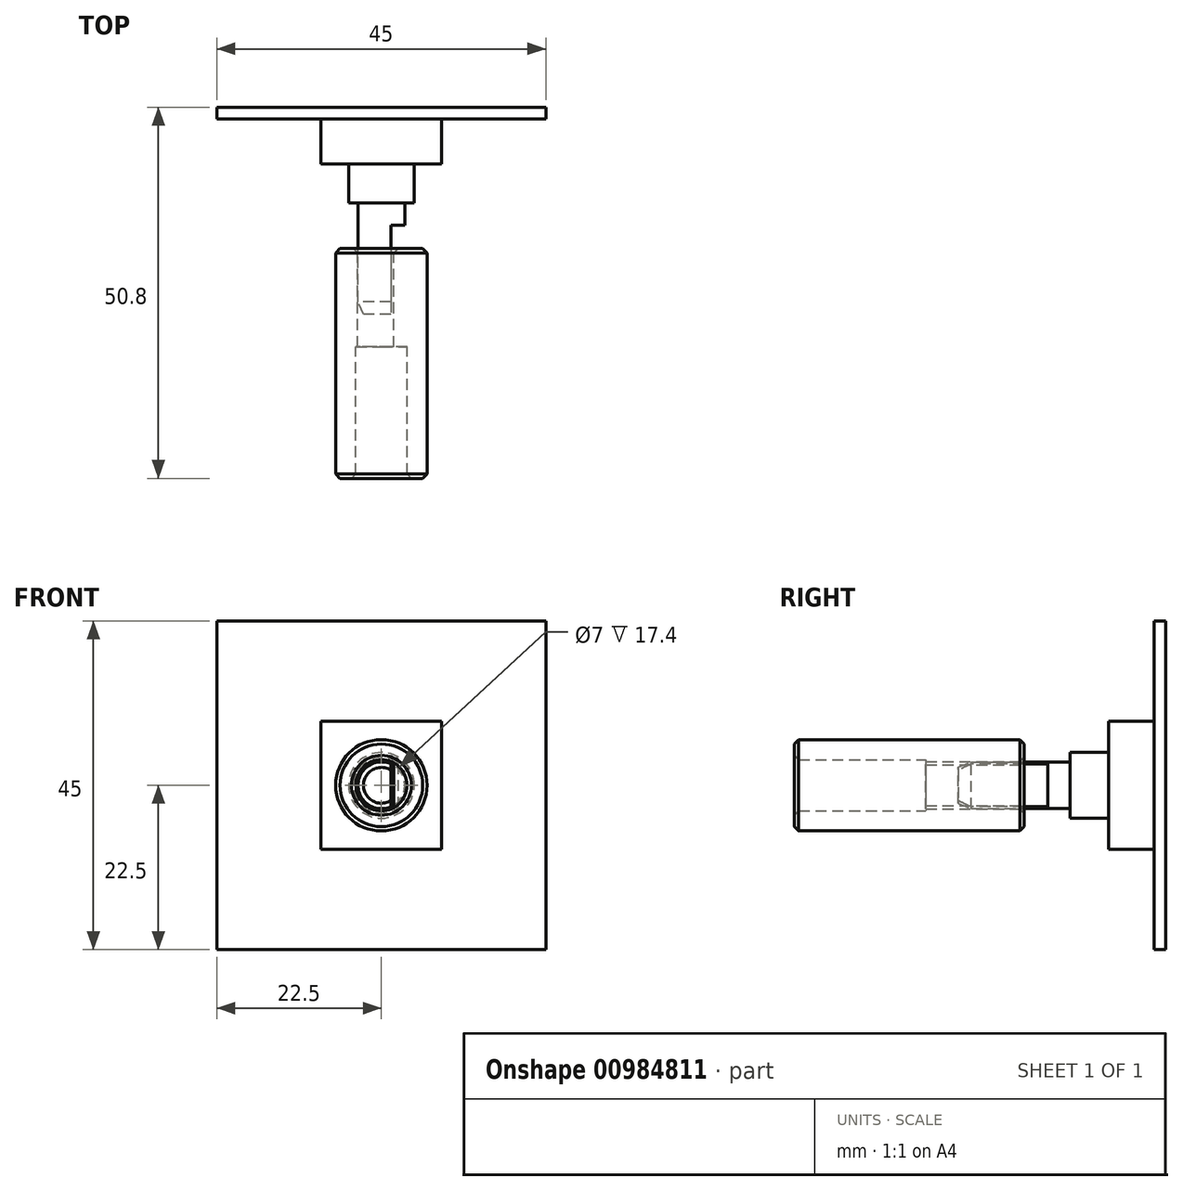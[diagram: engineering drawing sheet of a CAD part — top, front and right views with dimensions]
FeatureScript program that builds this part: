
annotation { "Feature Type Name" : "Feature", "Feature Type Description" : "" }
export const myFeature = defineFeature(function(context is Context, id is Id, definition is map)
    precondition{}
    {
        {
            var Q0;
            Q0=qCreatedBy(makeId("Front.planeOp"),FACE);
            var sketch = newSketch(context, id + "F0", { "sketchPlane" : qUnion([Q0])});
            skLineSegment(sketch, "E0.bottom", {"start": v(22.5, 22.5) * mm, "end": v(-22.5, 22.5) * mm});
            skLineSegment(sketch, "E0.top", {"start": v(22.5, -22.5) * mm, "end": v(-22.5, -22.5) * mm});
            skLineSegment(sketch, "E0.left", {"start": v(22.5, 22.5) * mm, "end": v(22.5, -22.5) * mm});
            skLineSegment(sketch, "E0.right", {"start": v(-22.5, 22.5) * mm, "end": v(-22.5, -22.5) * mm});
            skPoint(sketch, "E0.middle", {"position": v(0, 0) * mm});
            skSolve(sketch);
        }
        {
            var Q0;
            Q0 = qSketchRegion(id + "F0", true);
            extrude(context, id + "F1", {"entities" : qUnion([Q0]), "oppositeDirection" : true, "depth" : 1.6 * mm, "offsetDistance" : 25 * mm});
        }
        {
            var Q0;
            Q0=makeQuery(id+"F1.opExtrude","CAP_FACE",FACE,{"disambiguationData":[OSD([sQuery(id+"F0.wireOp",EDGE,"E0.bottom"),sQuery(id+"F0.wireOp",EDGE,"E0.top"),sQuery(id+"F0.wireOp",EDGE,"E0.left"),sQuery(id+"F0.wireOp",EDGE,"E0.right")])],"isStart":true});
            var sketch = newSketch(context, id + "F2", { "sketchPlane" : qUnion([Q0])});
            skLineSegment(sketch, "E1.bottom", {"start": v(8.25, 8.75) * mm, "end": v(-8.25, 8.75) * mm});
            skLineSegment(sketch, "E1.top", {"start": v(8.25, -8.75) * mm, "end": v(-8.25, -8.75) * mm});
            skLineSegment(sketch, "E1.left", {"start": v(8.25, 8.75) * mm, "end": v(8.25, -8.75) * mm});
            skLineSegment(sketch, "E1.right", {"start": v(-8.25, 8.75) * mm, "end": v(-8.25, -8.75) * mm});
            skPoint(sketch, "E1.middle", {"position": v(0, 0) * mm});
            skSolve(sketch);
        }
        {
            var Q0;
            Q0 = qSketchRegion(id + "F2", true);
            extrude(context, id + "F3", {"entities" : qUnion([Q0]), "operationType" : NewBodyOperationType.ADD, "depth" : 6.2 * mm, "offsetDistance" : 25 * mm});
        }
        {
            var Q0;
            Q0=makeQuery(id+"F3.opExtrude","CAP_FACE",FACE,{"disambiguationData":[OSD([sQuery(id+"F2.wireOp",EDGE,"E1.bottom"),sQuery(id+"F2.wireOp",EDGE,"E1.top"),sQuery(id+"F2.wireOp",EDGE,"E1.left"),sQuery(id+"F2.wireOp",EDGE,"E1.right")])],"isStart":false});
            var sketch = newSketch(context, id + "F4", { "sketchPlane" : qUnion([Q0])});
            skCircle(sketch, "E2", {"center": v(0, 0) * mm, "radius": 4.5 * mm});
            skSolve(sketch);
        }
        {
            var Q0;
            Q0 = qSketchRegion(id + "F4", true);
            extrude(context, id + "F5", {"entities" : qUnion([Q0]), "operationType" : NewBodyOperationType.ADD, "depth" : 5.3 * mm, "offsetDistance" : 25 * mm});
        }
        {
            var Q0;
            Q0=makeQuery(id+"F5.opExtrude","CAP_FACE",FACE,{"disambiguationData":[OSD([sQuery(id+"F4.wireOp",EDGE,"E2")])],"isStart":false});
            var sketch = newSketch(context, id + "F6", { "sketchPlane" : qUnion([Q0])});
            skCircle(sketch, "E3", {"center": v(0, 0) * mm, "radius": 3.2 * mm});
            skSolve(sketch);
        }
        {
            var Q0;
            Q0 = qSketchRegion(id + "F6", true);
            extrude(context, id + "F7", {"entities" : qUnion([Q0]), "operationType" : NewBodyOperationType.ADD, "depth" : 15.25 * mm, "offsetDistance" : 25 * mm});
        }
        {
            var Q0;
            Q0=makeQuery(id+"F7.opExtrude","CAP_FACE",FACE,{"disambiguationData":[OSD([sQuery(id+"F6.wireOp",EDGE,"E3")])],"isStart":false});
            var sketch = newSketch(context, id + "F8", { "sketchPlane" : qUnion([Q0])});
            skArc(sketch, "E4.1", {"start": v(1.3, -2.92) * mm, "mid": v(3.2, 0) * mm, "end": v(1.3, 2.92) * mm});
            skLineSegment(sketch, "E5", {"start": v(1.3, 2.92) * mm, "end": v(1.3, -2.92) * mm});
            skSolve(sketch);
        }
        {
            var Q0;
            Q0 = qSketchRegion(id + "F8", true);
            extrude(context, id + "F9", {"entities" : qUnion([Q0]), "operationType" : NewBodyOperationType.REMOVE, "oppositeDirection" : true, "depth" : 12.2 * mm, "offsetDistance" : 25 * mm});
        }
        {
            var Q0;
            Q0=qCreatedBy(makeId("Top.planeOp"),FACE);
            var sketch = newSketch(context, id + "F10", { "sketchPlane" : qUnion([Q0])});
            skLineSegment(sketch, "E6", {"start": v(-3.2, -25) * mm, "end": v(-3.2, -26.75) * mm});
            skLineSegment(sketch, "E7", {"start": v(-3.2, -26.75) * mm, "end": v(-2.45, -26.75) * mm});
            skLineSegment(sketch, "E8", {"start": v(-2.45, -26.75) * mm, "end": v(-3.2, -25) * mm});
            skLineSegment(sketch, "E9", {"start": v(0, -26.75) * mm, "end": v(0, 0) * mm, "construction": true});
            skSolve(sketch);
        }
        {
            var Q0;
            Q0 = qSketchRegion(id + "F10", true);
            var Q1;
            Q1=sQuery(id+"F10.wireOp",EDGE,"E9");
            var Q2;
            Q2=sQuery(id+"F10.wireOp",EDGE,"E6");
            var Q3;
            Q3=sQuery(id+"F10.wireOp",EDGE,"E8");
            var Q4;
            Q4=sQuery(id+"F10.wireOp",EDGE,"E7");
            var Q5;
            Q5=sQuery(id+"F10.wireOp",EDGE,"E9");
            revolve(context, id + "F11", {"operationType" : NewBodyOperationType.REMOVE, "surfaceOperationType" : NewSurfaceOperationType.NEW, "entities" : qUnion([Q0]), "surfaceEntities" : qUnion([Q1, Q2, Q3, Q4]), "axis" : qUnion([Q5]), "revolveType" : RevolveType.FULL, "oppositeDirection" : true});
        }
        {
            var Q0;
            Q0=qCreatedBy(makeId("Right.planeOp"),FACE);
            var sketch = newSketch(context, id + "F12", { "sketchPlane" : qUnion([Q0])});
            skLineSegment(sketch, "E10", {"start": v(0, 0) * mm, "end": v(-106.64, 0) * mm, "construction": true});
            skLineSegment(sketch, "E11", {"start": v(-73.58, -21.29) * mm, "end": v(-73.58, 21.29) * mm, "construction": true});
            skPoint(sketch, "E12", {"position": v(-73.58, 0) * mm});
            skLineSegment(sketch, "E13.bottom", {"start": v(-47.64, -8) * mm, "end": v(-42.64, -8) * mm});
            skLineSegment(sketch, "E13.top", {"start": v(-47.64, 8) * mm, "end": v(-42.64, 8) * mm});
            skLineSegment(sketch, "E13.left", {"start": v(-47.64, -8) * mm, "end": v(-47.64, 8) * mm});
            skLineSegment(sketch, "E13.right", {"start": v(-42.64, -8) * mm, "end": v(-42.64, 8) * mm});
            skPoint(sketch, "E13.middle", {"position": v(-45.14, 0) * mm});
            skLineSegment(sketch, "E14.bottom", {"start": v(-65.9, -8) * mm, "end": v(-60.9, -8) * mm});
            skLineSegment(sketch, "E14.top", {"start": v(-65.9, 8) * mm, "end": v(-60.9, 8) * mm});
            skLineSegment(sketch, "E14.left", {"start": v(-65.9, -8) * mm, "end": v(-65.9, 8) * mm});
            skLineSegment(sketch, "E14.right", {"start": v(-60.9, -8) * mm, "end": v(-60.9, 8) * mm});
            skPoint(sketch, "E14.middle", {"position": v(-63.4, 0) * mm});
            skLineSegment(sketch, "E15.bottom", {"start": v(-113.34, -35.98) * mm, "end": v(-99.95, -35.98) * mm});
            skLineSegment(sketch, "E15.top", {"start": v(-113.34, 35.98) * mm, "end": v(-99.95, 35.98) * mm});
            skLineSegment(sketch, "E15.left", {"start": v(-113.34, -35.98) * mm, "end": v(-113.34, 35.98) * mm});
            skLineSegment(sketch, "E15.right", {"start": v(-99.95, -35.98) * mm, "end": v(-99.95, 35.98) * mm});
            skPoint(sketch, "E15.middle", {"position": v(-106.64, 0) * mm});
            skSolve(sketch);
        }
        {
            var Q0;
            Q0=qCreatedBy(makeId("Right.planeOp"),FACE);
            var sketch = newSketch(context, id + "F13", { "sketchPlane" : qUnion([Q0])});
            skCircle(sketch, "E16.cCircle", {"center": v(-20.5, 0) * mm, "radius": 15.43 * mm, "construction": true});
            skLineSegment(sketch, "E16.0", {"start": v(-29.4, 15.43) * mm, "end": v(-11.6, 15.43) * mm, "construction": true});
            skLineSegment(sketch, "E16.1", {"start": v(-11.6, 15.43) * mm, "end": v(-2.69, 0) * mm, "construction": true});
            skLineSegment(sketch, "E16.2", {"start": v(-2.69, 0) * mm, "end": v(-11.6, -15.42) * mm, "construction": true});
            skLineSegment(sketch, "E16.3", {"start": v(-11.6, -15.42) * mm, "end": v(-29.4, -15.42) * mm, "construction": true});
            skLineSegment(sketch, "E16.4", {"start": v(-29.4, -15.42) * mm, "end": v(-38.31, 0) * mm, "construction": true});
            skLineSegment(sketch, "E16.5", {"start": v(-38.31, 0) * mm, "end": v(-29.4, 15.43) * mm, "construction": true});
            skPoint(sketch, "E16.0.midPoint", {"position": v(-20.5, 15.43) * mm});
            skLineSegment(sketch, "E17.bottom", {"start": v(-10.5, 10) * mm, "end": v(-30.5, 10) * mm, "construction": true});
            skLineSegment(sketch, "E17.top", {"start": v(-10.5, -10) * mm, "end": v(-30.5, -10) * mm, "construction": true});
            skLineSegment(sketch, "E17.left", {"start": v(-10.5, 10) * mm, "end": v(-10.5, -10) * mm, "construction": true});
            skLineSegment(sketch, "E17.right", {"start": v(-30.5, 10) * mm, "end": v(-30.5, -10) * mm, "construction": true});
            skCircle(sketch, "E18", {"center": v(-20.5, 0) * mm, "radius": 17 * mm, "construction": true});
            skLineSegment(sketch, "E19.bottom", {"start": v(-49, 16.55) * mm, "end": v(-45.5, 16.55) * mm, "construction": true});
            skLineSegment(sketch, "E19.top", {"start": v(-49, -16.55) * mm, "end": v(-45.5, -16.55) * mm, "construction": true});
            skLineSegment(sketch, "E19.left", {"start": v(-49, 16.55) * mm, "end": v(-49, 14.9) * mm, "construction": true});
            skLineSegment(sketch, "E19.right", {"start": v(-45.5, 16.55) * mm, "end": v(-45.5, -16.55) * mm, "construction": true});
            skLineSegment(sketch, "E20", {"start": v(-49.7, 14.9) * mm, "end": v(-49.7, -14.9) * mm, "construction": true});
            skLineSegment(sketch, "E21.trimOffspring", {"start": v(-49, -14.9) * mm, "end": v(-49, -16.55) * mm, "construction": true});
            skPoint(sketch, "E22", {"position": v(-45.5, 0) * mm});
            skLineSegment(sketch, "E23", {"start": v(-49.7, -14.9) * mm, "end": v(-47.5, -14.9) * mm, "construction": true});
            skLineSegment(sketch, "E24", {"start": v(-47.5, -14.9) * mm, "end": v(-47.5, 14.9) * mm, "construction": true});
            skLineSegment(sketch, "E25", {"start": v(-47.5, 14.9) * mm, "end": v(-49.7, 14.9) * mm, "construction": true});
            skLineSegment(sketch, "E26", {"start": v(-47.5, 3.5) * mm, "end": v(-31.7, 3.5) * mm, "construction": true});
            skLineSegment(sketch, "E27", {"start": v(-31.7, 3.5) * mm, "end": v(-31.7, -3.5) * mm, "construction": true});
            skLineSegment(sketch, "E28", {"start": v(-31.7, -3.5) * mm, "end": v(-47.5, -3.5) * mm, "construction": true});
            skPoint(sketch, "E29", {"position": v(-31.7, 0) * mm});
            skSolve(sketch);
        }
        {
            var Q0;
            Q0=qCreatedBy(makeId("Right.planeOp"),FACE);
            var sketch = newSketch(context, id + "F14", { "sketchPlane" : qUnion([Q0])});
            skLineSegment(sketch, "E30", {"start": v(-17.75, 3.25) * mm, "end": v(-17.75, 6.25) * mm});
            skLineSegment(sketch, "E31", {"start": v(-17.75, 6.25) * mm, "end": v(-49.2, 6.25) * mm});
            skLineSegment(sketch, "E32", {"start": v(-49.2, 6.25) * mm, "end": v(-49.2, 3.5) * mm});
            skLineSegment(sketch, "E33", {"start": v(-49.2, 3.5) * mm, "end": v(-31.2, 3.5) * mm});
            skLineSegment(sketch, "E34", {"start": v(-28.75, 3.25) * mm, "end": v(-17.75, 3.25) * mm});
            skLineSegment(sketch, "E35.0", {"start": v(0, 0) * mm, "end": v(-106.64, 0) * mm, "construction": true});
            skPoint(sketch, "E36", {"position": v(-11.5, 3.2) * mm});
            skLineSegment(sketch, "E37", {"start": v(-28.75, 3.25) * mm, "end": v(-28.75, 0) * mm});
            skLineSegment(sketch, "E38", {"start": v(-28.75, 0) * mm, "end": v(-31.2, 0) * mm});
            skLineSegment(sketch, "E39", {"start": v(-31.2, 0) * mm, "end": v(-31.2, 3.5) * mm});
            skSolve(sketch);
        }
        {
            var Q0;
            Q0 = qSketchRegion(id + "F14", true);
            var Q1;
            Q1=sQuery(id+"F14.wireOp",EDGE,"E38");
            revolve(context, id + "F15", {"surfaceOperationType" : NewSurfaceOperationType.NEW, "entities" : qUnion([Q0]), "axis" : qUnion([Q1]), "revolveType" : RevolveType.FULL});
        }
        {
            var Q0;
            Q0=makeQuery(id+"F15.opRevolve","SWEPT_FACE",FACE,{"disambiguationData":[OSD([sQuery(id+"F14.wireOp",EDGE,"E30")])]});
            var sketch = newSketch(context, id + "F16", { "sketchPlane" : qUnion([Q0])});
            skLineSegment(sketch, "E40", {"start": v(-1.7, 2.77) * mm, "end": v(-1.7, -2.77) * mm});
            skArc(sketch, "E41.0", {"start": v(-1.7, 2.77) * mm, "mid": v(-3.25, 0) * mm, "end": v(-1.7, -2.77) * mm});
            skSolve(sketch);
        }
        {
            var Q0;
            Q0 = qSketchRegion(id + "F16", true);
            var Q1;
            Q1=makeQuery(id+"F15.opRevolve","SWEPT_FACE",FACE,{"disambiguationData":[OSD([sQuery(id+"F14.wireOp",EDGE,"E37")])]});
            extrude(context, id + "F17", {"entities" : qUnion([Q0]), "operationType" : NewBodyOperationType.ADD, "endBound" : BoundingType.UP_TO_SURFACE, "oppositeDirection" : true, "depth" : 25 * mm, "endBoundEntityFace" : qUnion([Q1]), "offsetDistance" : 25 * mm});
        }
        {
            var Q0;
            Q0=makeQuery(id+"F15.opRevolve","SWEPT_EDGE",EDGE,{"disambiguationData":[OSD([sQuery(id+"F14.wireOp",EDGE,"E30"),sQuery(id+"F14.wireOp",EDGE,"E31")])]});
            var Q1;
            Q1=makeQuery(id+"F15.opRevolve","SWEPT_EDGE",EDGE,{"disambiguationData":[OSD([sQuery(id+"F14.wireOp",EDGE,"E31"),sQuery(id+"F14.wireOp",EDGE,"E32")])]});
            var Q2;
            Q2=makeQuery(id+"F15.opRevolve","SWEPT_EDGE",EDGE,{"disambiguationData":[OSD([sQuery(id+"F14.wireOp",EDGE,"E32"),sQuery(id+"F14.wireOp",EDGE,"E33")])]});
            var Q3;
            Q3=makeQuery(id+"F15.opRevolve","SWEPT_EDGE",EDGE,{"disambiguationData":[OSD([sQuery(id+"F14.wireOp",EDGE,"E30"),sQuery(id+"F14.wireOp",EDGE,"E34")])]});
            var Q4;
            Q4=makeQuery(id+"F17.opExtrude","CAP_EDGE",EDGE,{"disambiguationData":[OSD([sQuery(id+"F16.wireOp",EDGE,"E40")])],"isStart":true});
            chamfer(context, id + "F18", {"entities" : qUnion([Q0, Q1, Q2, Q3, Q4]), "width" : .6 * mm, "tangentPropagation" : true});
        }
        {
            var Q0;
            Q0=makeQuery(id+"F15.opRevolve","SWEPT_FACE",FACE,{"disambiguationData":[OSD([sQuery(id+"F14.wireOp",EDGE,"E37")])]});
            extrude(context, id + "F19", {"entities" : qUnion([Q0]), "operationType" : NewBodyOperationType.REMOVE, "oppositeDirection" : true, "depth" : 25 * mm, "offsetDistance" : 25 * mm});
        }
    });
